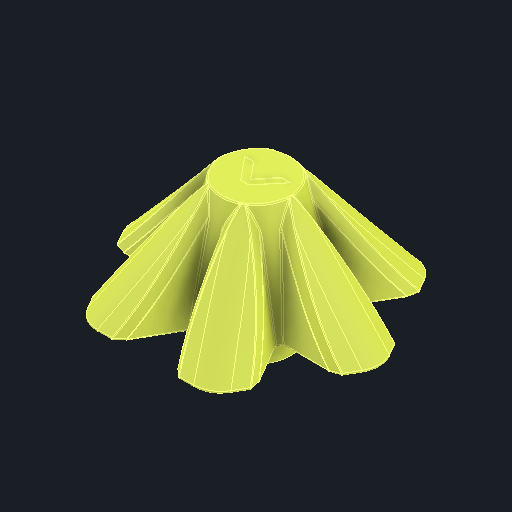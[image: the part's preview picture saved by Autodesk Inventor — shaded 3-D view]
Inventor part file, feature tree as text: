
AUTODESK INVENTOR PART (.ipt)
format: ipt  version: 2025 (Build 290162000, 162)  size: 3,516,928 bytes
history: native  units: in
note: dims shown in document units (in); Inventor stores cm internally (conversion verified against a paired STEP export)
features: fillet x1
ambient origin geometry x8: Origin, YZ Plane, XZ Plane, XY Plane, X Axis, Y Axis, Z Axis, Center Point
bodies: Solid1 (feature_tree)
feature tree (1):
  fillet  "Fillet156"  [1 undecoded]
note: 1 required parameter value undecoded (feature->parameter linkage not recoverable at this tier; creation-order binding heuristic only, values carry confidence <= 0.55)
